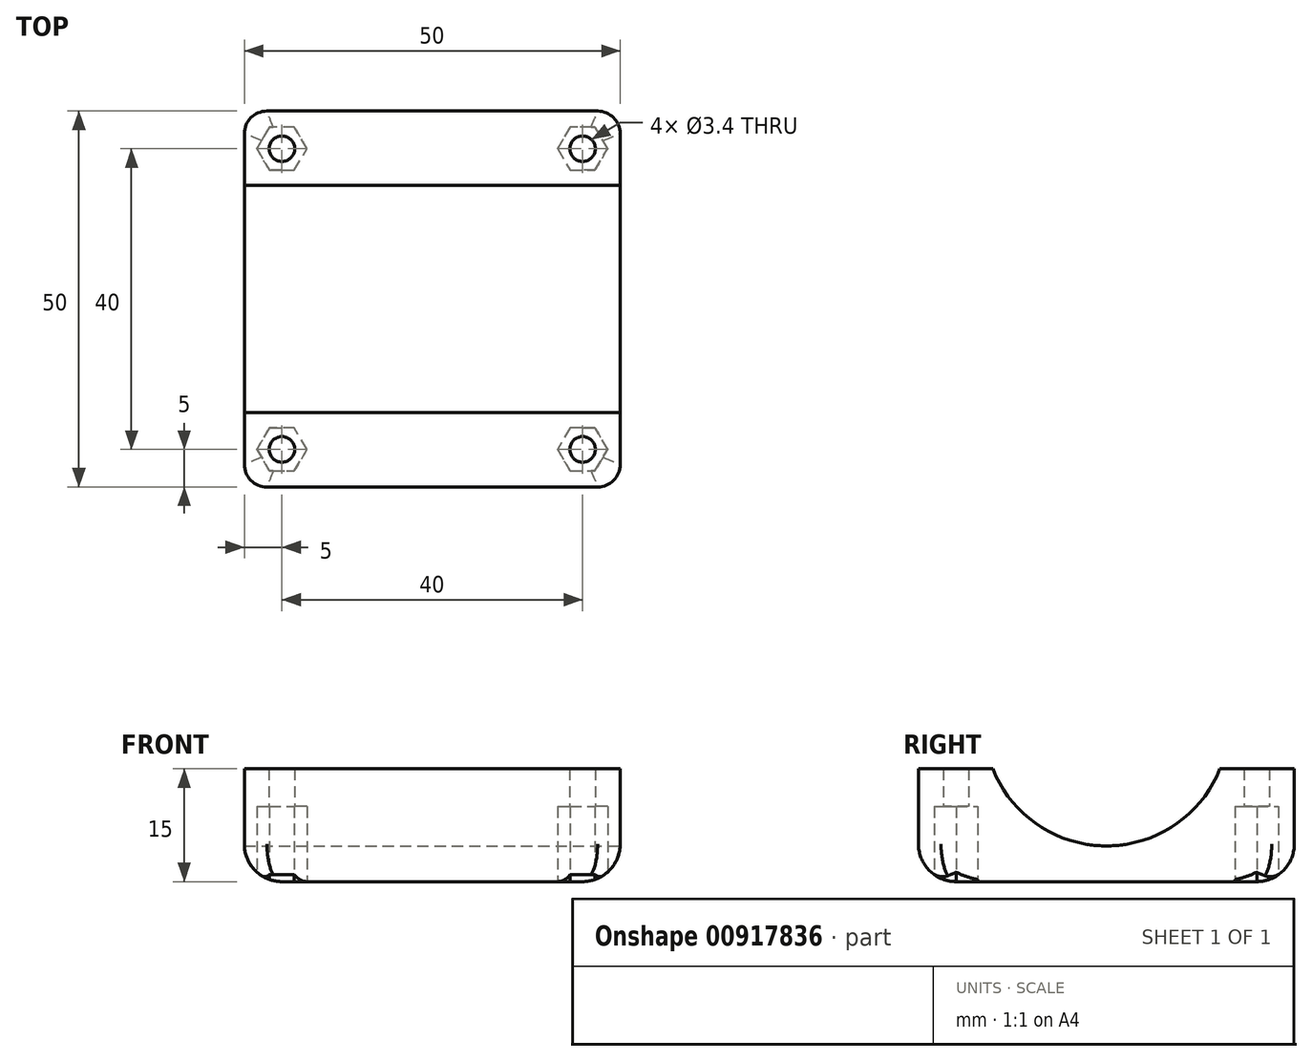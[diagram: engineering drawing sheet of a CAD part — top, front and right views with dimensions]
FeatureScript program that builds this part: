
annotation { "Feature Type Name" : "Feature", "Feature Type Description" : "" }
export const myFeature = defineFeature(function(context is Context, id is Id, definition is map)
    precondition{}
    {
        {
            var Q0;
            Q0=qCreatedBy(makeId("Top.planeOp"),FACE);
            var sketch = newSketch(context, id + "F0", { "sketchPlane" : qUnion([Q0])});
            skLineSegment(sketch, "E0.bottom", {"start": v(-25, 25) * mm, "end": v(25, 25) * mm});
            skLineSegment(sketch, "E0.top", {"start": v(-25, -25) * mm, "end": v(25, -25) * mm});
            skLineSegment(sketch, "E0.left", {"start": v(-25, 25) * mm, "end": v(-25, -25) * mm});
            skLineSegment(sketch, "E0.right", {"start": v(25, 25) * mm, "end": v(25, -25) * mm});
            skSolve(sketch);
        }
        {
            var Q0;
            Q0 = qSketchRegion(id + "F0", true);
            extrude(context, id + "F1", {"entities" : qUnion([Q0]), "depth" : 15 * mm, "offsetDistance" : 25 * mm});
        }
        {
            var Q0;
            Q0=qCreatedBy(makeId("Right.planeOp"),FACE);
            var sketch = newSketch(context, id + "F2", { "sketchPlane" : qUnion([Q0])});
            skCircle(sketch, "E1", {"center": v(0, 21) * mm, "radius": 16.25 * mm});
            skSolve(sketch);
        }
        {
            var Q0;
            Q0 = qSketchRegion(id + "F2", true);
            extrude(context, id + "F3", {"entities" : qUnion([Q0]), "operationType" : NewBodyOperationType.REMOVE, "endBound" : BoundingType.SYMMETRIC, "oppositeDirection" : true, "depth" : 50 * mm, "offsetDistance" : 25 * mm});
        }
        {
            var Q0;
            Q0=makeQuery(id+"F1.opExtrude","SWEPT_EDGE",EDGE,{"disambiguationData":[OSD([sQuery(id+"F0.wireOp",EDGE,"E0.top"),sQuery(id+"F0.wireOp",EDGE,"E0.left")])]});
            var Q1;
            Q1=makeQuery(id+"F1.opExtrude","SWEPT_EDGE",EDGE,{"disambiguationData":[OSD([sQuery(id+"F0.wireOp",EDGE,"E0.top"),sQuery(id+"F0.wireOp",EDGE,"E0.right")])]});
            var Q2;
            Q2=makeQuery(id+"F1.opExtrude","SWEPT_EDGE",EDGE,{"disambiguationData":[OSD([sQuery(id+"F0.wireOp",EDGE,"E0.bottom"),sQuery(id+"F0.wireOp",EDGE,"E0.right")])]});
            var Q3;
            Q3=makeQuery(id+"F1.opExtrude","SWEPT_EDGE",EDGE,{"disambiguationData":[OSD([sQuery(id+"F0.wireOp",EDGE,"E0.bottom"),sQuery(id+"F0.wireOp",EDGE,"E0.left")])]});
            fillet(context, id + "F4", {"entities" : qUnion([Q0, Q1, Q2, Q3]), "radius" : 3 * mm, "tangentPropagation" : true, "allowEdgeOverflow" : false});
        }
        {
            var Q0;
            Q0=makeQuery(id+"F1.opExtrude","CAP_FACE",FACE,{"disambiguationData":[OSD([sQuery(id+"F0.wireOp",EDGE,"E0.bottom"),sQuery(id+"F0.wireOp",EDGE,"E0.top"),sQuery(id+"F0.wireOp",EDGE,"E0.left"),sQuery(id+"F0.wireOp",EDGE,"E0.right")])],"isStart":true});
            var sketch = newSketch(context, id + "F5", { "sketchPlane" : qUnion([Q0])});
            skPoint(sketch, "E2", {"position": v(-20, 20) * mm});
            skPoint(sketch, "E3", {"position": v(20, 20) * mm});
            skPoint(sketch, "E4", {"position": v(20, -20) * mm});
            skPoint(sketch, "E5", {"position": v(-20, -20) * mm});
            skSolve(sketch);
        }
        {
            var Q0;
            {var subQ3=sQuery(id+"F0.wireOp",EDGE,"E0.bottom");Q0=makeQuery(id+"F5.imprint","IMPRINT",FACE,{"disambiguationData":[TD([[makeQuery(id+"F5.imprint","IMPRINT",EDGE,{"derivedFrom":makeQuery(id+"F1.opExtrude","CAP_EDGE",EDGE,{"disambiguationData":[OSD([subQ3])],"isStart":true})}),1.0]])]});}
            var sketch = newSketch(context, id + "F6", { "sketchPlane" : qUnion([Q0])});
            skPoint(sketch, "E6.0", {"position": v(-20, 20) * mm});
            skPoint(sketch, "E7.0", {"position": v(20, 20) * mm});
            skPoint(sketch, "E8.0", {"position": v(20, -20) * mm});
            skPoint(sketch, "E9.0", {"position": v(-20, -20) * mm});
            skCircle(sketch, "E10", {"center": v(-20, 20) * mm, "radius": 1.7 * mm});
            skCircle(sketch, "E11", {"center": v(20, 20) * mm, "radius": 1.7 * mm});
            skCircle(sketch, "E12", {"center": v(20, -20) * mm, "radius": 1.7 * mm});
            skCircle(sketch, "E13", {"center": v(-20, -20) * mm, "radius": 1.7 * mm});
            skSolve(sketch);
        }
        {
            var Q0;
            Q0 = qSketchRegion(id + "F6", true);
            extrude(context, id + "F7", {"entities" : qUnion([Q0]), "operationType" : NewBodyOperationType.REMOVE, "endBound" : BoundingType.THROUGH_ALL, "oppositeDirection" : true, "depth" : 25 * mm, "offsetDistance" : 25 * mm});
        }
        {
            var Q0;
            {var subQ3=sQuery(id+"F0.wireOp",EDGE,"E0.bottom");Q0=makeQuery(id+"F5.imprint","IMPRINT",FACE,{"disambiguationData":[TD([[makeQuery(id+"F5.imprint","IMPRINT",EDGE,{"derivedFrom":makeQuery(id+"F1.opExtrude","CAP_EDGE",EDGE,{"disambiguationData":[OSD([subQ3])],"isStart":true})}),1.0]])]});}
            var sketch = newSketch(context, id + "F8", { "sketchPlane" : qUnion([Q0])});
            skPoint(sketch, "E14.0", {"position": v(-20, 20) * mm});
            skCircle(sketch, "E15.cCircle", {"center": v(-20, 20) * mm, "radius": 2.87 * mm, "construction": true});
            skLineSegment(sketch, "E15.0", {"start": v(-18.34, 17.13) * mm, "end": v(-21.66, 17.13) * mm});
            skLineSegment(sketch, "E15.1", {"start": v(-21.66, 17.13) * mm, "end": v(-23.32, 20) * mm});
            skLineSegment(sketch, "E15.2", {"start": v(-23.32, 20) * mm, "end": v(-21.66, 22.88) * mm});
            skLineSegment(sketch, "E15.3", {"start": v(-21.66, 22.88) * mm, "end": v(-18.34, 22.88) * mm});
            skLineSegment(sketch, "E15.4", {"start": v(-18.34, 22.88) * mm, "end": v(-16.68, 20) * mm});
            skLineSegment(sketch, "E15.5", {"start": v(-16.68, 20) * mm, "end": v(-18.34, 17.13) * mm});
            skPoint(sketch, "E15.0.midPoint", {"position": v(-20, 17.13) * mm});
            skPoint(sketch, "E16.0", {"position": v(20, 20) * mm});
            skPoint(sketch, "E17.0", {"position": v(20, -20) * mm});
            skPoint(sketch, "E18.0", {"position": v(-20, -20) * mm});
            skCircle(sketch, "E19.cCircle", {"center": v(20, 20) * mm, "radius": 2.88 * mm, "construction": true});
            skPoint(sketch, "E19.cCircle.perimeterSnap0", {"position": v(-17.51, 18.56) * mm});
            skLineSegment(sketch, "E19.0", {"start": v(23.32, 20) * mm, "end": v(21.66, 17.12) * mm});
            skLineSegment(sketch, "E19.1", {"start": v(21.66, 17.13) * mm, "end": v(18.34, 17.12) * mm});
            skLineSegment(sketch, "E19.2", {"start": v(18.34, 17.12) * mm, "end": v(16.68, 20) * mm});
            skLineSegment(sketch, "E19.3", {"start": v(16.68, 20) * mm, "end": v(18.34, 22.88) * mm});
            skLineSegment(sketch, "E19.4", {"start": v(18.34, 22.88) * mm, "end": v(21.66, 22.88) * mm});
            skLineSegment(sketch, "E19.5", {"start": v(21.66, 22.88) * mm, "end": v(23.32, 20) * mm});
            skPoint(sketch, "E19.0.midPoint", {"position": v(22.49, 18.56) * mm});
            skPoint(sketch, "E19.0.midPoint.positionSnap0", {"position": v(-17.51, 18.56) * mm});
            skCircle(sketch, "E20.cCircle", {"center": v(-20, -20) * mm, "radius": 2.88 * mm, "construction": true});
            skLineSegment(sketch, "E20.0", {"start": v(-16.68, -20) * mm, "end": v(-18.34, -22.88) * mm});
            skLineSegment(sketch, "E20.1", {"start": v(-18.34, -22.87) * mm, "end": v(-21.66, -22.88) * mm});
            skLineSegment(sketch, "E20.2", {"start": v(-21.66, -22.88) * mm, "end": v(-23.32, -20) * mm});
            skLineSegment(sketch, "E20.3", {"start": v(-23.32, -20) * mm, "end": v(-21.66, -17.13) * mm});
            skLineSegment(sketch, "E20.4", {"start": v(-21.66, -17.13) * mm, "end": v(-18.34, -17.12) * mm});
            skLineSegment(sketch, "E20.5", {"start": v(-18.34, -17.12) * mm, "end": v(-16.68, -20) * mm});
            skPoint(sketch, "E20.0.midPoint", {"position": v(-17.51, -21.44) * mm});
            skCircle(sketch, "E21.cCircle", {"center": v(20, -20) * mm, "radius": 2.88 * mm, "construction": true});
            skLineSegment(sketch, "E21.0", {"start": v(23.32, -20) * mm, "end": v(21.66, -22.87) * mm});
            skLineSegment(sketch, "E21.1", {"start": v(21.66, -22.87) * mm, "end": v(18.34, -22.88) * mm});
            skLineSegment(sketch, "E21.2", {"start": v(18.34, -22.88) * mm, "end": v(16.68, -20) * mm});
            skLineSegment(sketch, "E21.3", {"start": v(16.68, -20) * mm, "end": v(18.34, -17.13) * mm});
            skLineSegment(sketch, "E21.4", {"start": v(18.34, -17.13) * mm, "end": v(21.66, -17.12) * mm});
            skLineSegment(sketch, "E21.5", {"start": v(21.66, -17.12) * mm, "end": v(23.32, -20) * mm});
            skPoint(sketch, "E21.0.midPoint", {"position": v(22.49, -21.44) * mm});
            skSolve(sketch);
        }
        {
            var Q0;
            Q0 = qSketchRegion(id + "F8", true);
            extrude(context, id + "F9", {"entities" : qUnion([Q0]), "operationType" : NewBodyOperationType.REMOVE, "oppositeDirection" : true, "depth" : 10 * mm, "offsetDistance" : 25 * mm});
        }
        {
            var Q0;
            Q0=makeQuery(id+"F1.opExtrude","CAP_EDGE",EDGE,{"disambiguationData":[OSD([sQuery(id+"F0.wireOp",EDGE,"E0.right")])],"isStart":true});
            fillet(context, id + "F10", {"entities" : qUnion([Q0]), "radius" : 5 * mm, "tangentPropagation" : true, "allowEdgeOverflow" : false});
        }
    });
